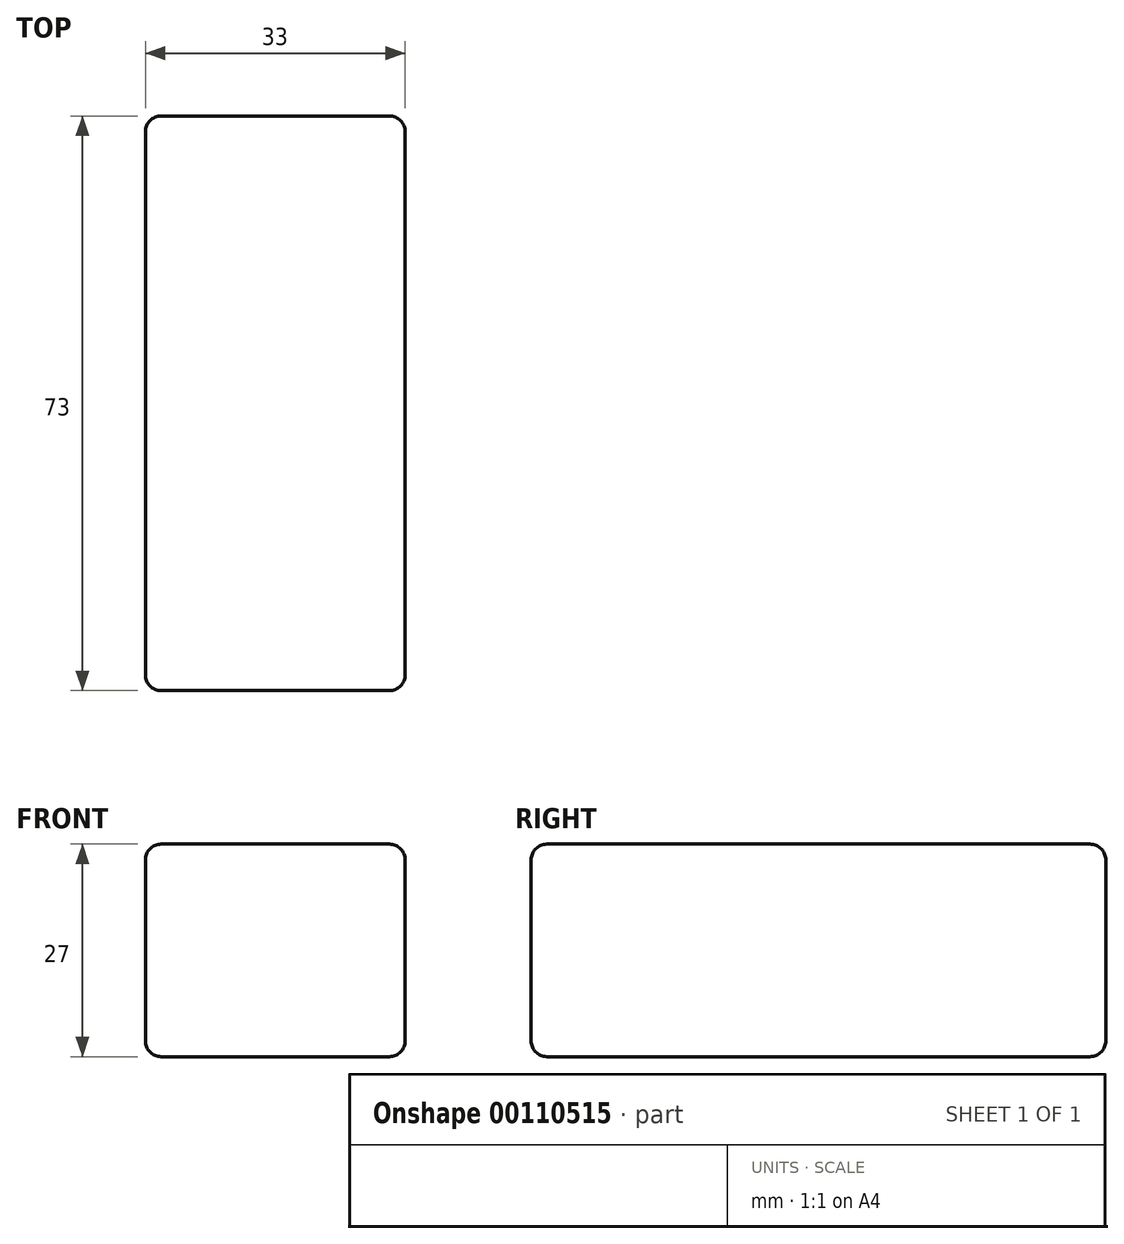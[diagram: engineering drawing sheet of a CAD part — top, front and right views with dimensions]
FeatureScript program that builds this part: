
annotation { "Feature Type Name" : "Feature", "Feature Type Description" : "" }
export const myFeature = defineFeature(function(context is Context, id is Id, definition is map)
    precondition{}
    {
        {
            var Q0;
            Q0=qCreatedBy(makeId("Top.planeOp"),FACE);
            var sketch = newSketch(context, id + "F0", { "sketchPlane" : qUnion([Q0])});
            skLineSegment(sketch, "E0.bottom", {"start": v(16.5, 36.5) * mm, "end": v(-16.5, 36.5) * mm});
            skLineSegment(sketch, "E0.top", {"start": v(16.5, -36.5) * mm, "end": v(-16.5, -36.5) * mm});
            skLineSegment(sketch, "E0.left", {"start": v(16.5, 36.5) * mm, "end": v(16.5, -36.5) * mm});
            skLineSegment(sketch, "E0.right", {"start": v(-16.5, 36.5) * mm, "end": v(-16.5, -36.5) * mm});
            skPoint(sketch, "E0.middle", {"position": v(0, 0) * mm});
            skSolve(sketch);
        }
        {
            var Q0;
            Q0 = qSketchRegion(id + "F0", true);
            extrude(context, id + "F1", {"entities" : qUnion([Q0]), "endBound" : BoundingType.SYMMETRIC, "depth" : 27 * mm});
        }
        {
            var Q0;
            Q0=makeQuery(id+"F1.opExtrude","CAP_FACE",FACE,{"disambiguationData":[OSD([sQuery(id+"F0.wireOp",EDGE,"E0.bottom"),sQuery(id+"F0.wireOp",EDGE,"E0.top"),sQuery(id+"F0.wireOp",EDGE,"E0.left"),sQuery(id+"F0.wireOp",EDGE,"E0.right")])],"isStart":false});
            var Q1;
            Q1=makeQuery(id+"F1.opExtrude","SWEPT_FACE",FACE,{"disambiguationData":[OSD([sQuery(id+"F0.wireOp",EDGE,"E0.left")])]});
            var Q2;
            Q2=makeQuery(id+"F1.opExtrude","SWEPT_FACE",FACE,{"disambiguationData":[OSD([sQuery(id+"F0.wireOp",EDGE,"E0.top")])]});
            var Q3;
            Q3=makeQuery(id+"F1.opExtrude","SWEPT_FACE",FACE,{"disambiguationData":[OSD([sQuery(id+"F0.wireOp",EDGE,"E0.right")])]});
            var Q4;
            Q4=makeQuery(id+"F1.opExtrude","SWEPT_FACE",FACE,{"disambiguationData":[OSD([sQuery(id+"F0.wireOp",EDGE,"E0.bottom")])]});
            var Q5;
            Q5=makeQuery(id+"F1.opExtrude","CAP_FACE",FACE,{"disambiguationData":[OSD([sQuery(id+"F0.wireOp",EDGE,"E0.bottom"),sQuery(id+"F0.wireOp",EDGE,"E0.top"),sQuery(id+"F0.wireOp",EDGE,"E0.left"),sQuery(id+"F0.wireOp",EDGE,"E0.right")])],"isStart":true});
            fillet(context, id + "F2", {"entities" : qUnion([Q0, Q1, Q2, Q3, Q4, Q5]), "radius" : 2 * mm, "tangentPropagation" : true, "allowEdgeOverflow" : false});
        }
    });
